# Revit family: Plymold-Essentials-Cebra-6_Seat_Wall-Quest-
name_source: partatom
category: Furniture
units: mm (PartAtom-declared; Revit-internal decimal feet)

## family parameters
Always vertical = Yes
Cut with Voids When Loaded = No
OmniClass Number = 23.40.20.00
OmniClass Title = General Furniture and Specialties
Room Calculation Point = No
Shared = No
Work Plane-Based = No

## types (4) — shared parameters
Assembly Code = E2020200
Back Finish = PLY - Onyx Black Powdercoat
Base Finish = PLY - Onyx Black Powdercoat
Cap Finish = PLY - Plastic Black
Default Elevation = 0"
Depth = 62"
Edge Finish = PLY - Plastic Black
Frame Finish = PLY - Onyx Black Powdercoat
Glides Finish = PLY - Plastic Black
Hardware Finish = PLY - Onyx Black Powdercoat
Height = 29 3/4"
Keynote = 12500
Manufacturer = Plymold
Revit Model Built By = https://www.servex-us.com
Seat Finish = PLY - Plastic Blue
Support Finish = PLY - Onyx Black Powdercoat
Sustainability = https://plymold.com
Top Finish = PLY - Wood Mahogany
Type Comments = Quest
URL = https://plymold.com
Width = 76"
zero-valued in all types: Cost

## per-type parameters (varying)
| type | DE | Description | PVC | TPD | VE |
| CEWL006DEQU | Yes | 6 Seat Wall Unit - Cebra® Cluster w/Bullnose Dur-A-Edge® Table Top Unit - 76”W x 66.25”D x 29.75”H | No | No | No |
| CEWL006TPDQU | No | 6 Seat Wall Unit - Cebra® Cluster w/Thin Dur-A-Edge® Table Top Unit - 76”W x 66.25”D x 29.75”H | No | Yes | No |
| CEWL006VEQU | No | 6 Seat Wall Unit - Cebra® Cluster w/ Vinyl Edge Table Top - 76”W x 66.25”D x 29.75”H | No | No | Yes |
| CEWL006PVCQU | No | 6 Seat Wall Unit - Cebra® Cluster w/ PVC Edge Table Top - 76”W x 66.25”D x 29.75”H | Yes | No | No |

note: column(s) folded — value = type name in every type: Model

## geometry (parser evidence)
native form markers: Sweep x16
no freeform markers — native parametric forms only
